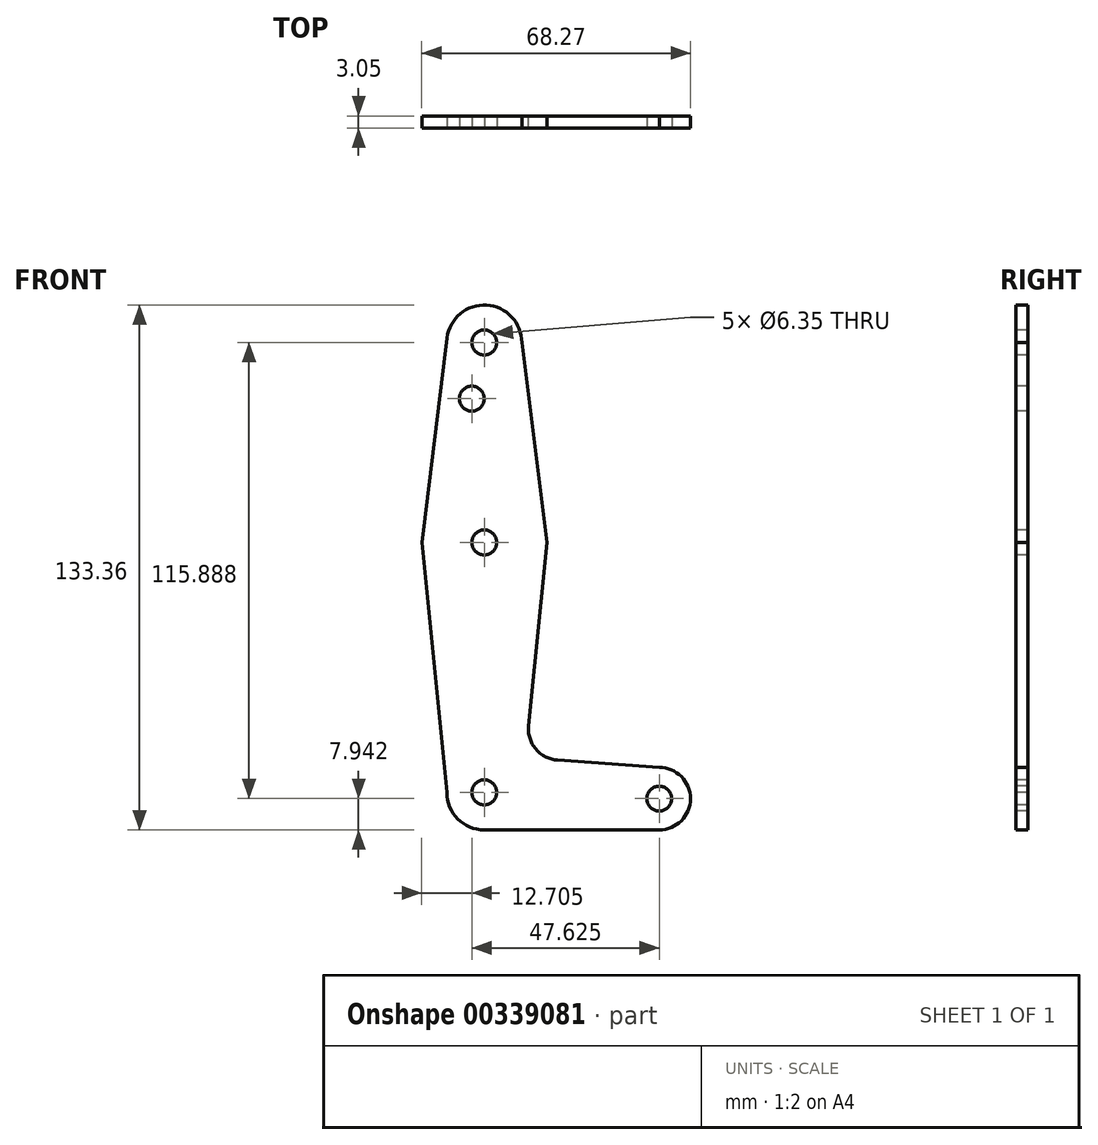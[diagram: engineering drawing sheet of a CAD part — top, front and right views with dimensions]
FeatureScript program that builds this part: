
annotation { "Feature Type Name" : "Feature", "Feature Type Description" : "" }
export const myFeature = defineFeature(function(context is Context, id is Id, definition is map)
    precondition{}
    {
        {
            var Q0;
            Q0=qCreatedBy(makeId("Front.planeOp"),FACE);
            var sketch = newSketch(context, id + "F0", { "sketchPlane" : qUnion([Q0])});
            skCircle(sketch, "E0", {"center": v(0, 0) * mm, "radius": 9.53 * mm});
            skCircle(sketch, "E1", {"center": v(0, 63.5) * mm, "radius": 15.88 * mm});
            skCircle(sketch, "E2", {"center": v(0, 114.3) * mm, "radius": 9.53 * mm});
            skCircle(sketch, "E3", {"center": v(44.45, -1.59) * mm, "radius": 7.94 * mm});
            skLineSegment(sketch, "E4", {"start": v(-15.87, 63.5) * mm, "end": v(-9.52, 0) * mm});
            skLineSegment(sketch, "E5", {"start": v(15.88, 63.5) * mm, "end": v(9.48, -0.94) * mm});
            skLineSegment(sketch, "E6", {"start": v(-15.87, 63.5) * mm, "end": v(-9.45, 115.47) * mm});
            skLineSegment(sketch, "E7", {"start": v(15.88, 63.5) * mm, "end": v(9.52, 114.3) * mm});
            skLineSegment(sketch, "E8", {"start": v(0.68, 9.5) * mm, "end": v(44.45, 6.35) * mm});
            skLineSegment(sketch, "E9", {"start": v(0, -9.53) * mm, "end": v(44.45, -9.52) * mm});
            skCircle(sketch, "E10", {"center": v(0, 114.3) * mm, "radius": 3.18 * mm});
            skCircle(sketch, "E11", {"center": v(0, 0) * mm, "radius": 3.18 * mm});
            skCircle(sketch, "E12", {"center": v(44.45, -1.59) * mm, "radius": 3.18 * mm});
            skCircle(sketch, "E13", {"center": v(0, 63.5) * mm, "radius": 3.18 * mm});
            skPoint(sketch, "E14.center.orphan", {"position": v(-3.18, 100.03) * mm});
            skCircle(sketch, "E15", {"center": v(-3.18, 100.03) * mm, "radius": 3.18 * mm});
            skLineSegment(sketch, "E16", {"start": v(0, 63.5) * mm, "end": v(0, 66.67) * mm});
            skSolve(sketch);
        }
        {
            var Q0;
            Q0=makeQuery(id+"F0.imprint","IMPRINT",FACE,{"disambiguationData":[TD([[makeQuery(id+"F0.imprint","IMPRINT",EDGE,{"derivedFrom":sQuery(id+"F0.wireOp",EDGE,"E15")}),-1.0]])]});
            var Q1;
            Q1=makeQuery(id+"F0.imprint","IMPRINT",FACE,{"disambiguationData":[TD([[makeQuery(id+"F0.imprint","IMPRINT",EDGE,{"derivedFrom":sQuery(id+"F0.wireOp",EDGE,"E10")}),-1.0]])]});
            var Q2;
            Q2=makeQuery(id+"F0.imprint","IMPRINT",FACE,{"disambiguationData":[TD([[makeQuery(id+"F0.imprint","IMPRINT",EDGE,{"derivedFrom":sQuery(id+"F0.wireOp",EDGE,"E13")}),-1.0]])]});
            var Q3;
            {var subQ5=sQuery(id+"F0.wireOp",EDGE,"E4");var subQ7=sQuery(id+"F0.wireOp",EDGE,"E0");var subQ8=makeQuery(id+"F0.imprint","INTERSECT",VERTEX,{"derivedFrom":[subQ7,subQ5]});Q3=makeQuery(id+"F0.imprint","IMPRINT",FACE,{"disambiguationData":[TD([[makeQuery(id+"F0.imprint","IMPRINT",EDGE,{"disambiguationData":[TD([[subQ8,1.0]])],"derivedFrom":subQ7}),-1.0]])]});}
            var Q4;
            {var subQ7=sQuery(id+"F0.wireOp",EDGE,"E9");Q4=makeQuery(id+"F0.imprint","IMPRINT",FACE,{"disambiguationData":[TD([[makeQuery(id+"F0.imprint","IMPRINT",EDGE,{"derivedFrom":subQ7}),1.0]])]});}
            var Q5;
            Q5=makeQuery(id+"F0.imprint","IMPRINT",FACE,{"disambiguationData":[TD([[makeQuery(id+"F0.imprint","IMPRINT",EDGE,{"derivedFrom":sQuery(id+"F0.wireOp",EDGE,"E12")}),-1.0]])]});
            var Q6;
            Q6=makeQuery(id+"F0.imprint","IMPRINT",FACE,{"disambiguationData":[TD([[makeQuery(id+"F0.imprint","IMPRINT",EDGE,{"derivedFrom":sQuery(id+"F0.wireOp",EDGE,"E11")}),-1.0]])]});
            var Q7;
            {var subQ0=sQuery(id+"F0.wireOp",EDGE,"E5");var subQ1=sQuery(id+"F0.wireOp",EDGE,"E0");var subQ2=makeQuery(id+"F0.imprint","INTERSECT",VERTEX,{"derivedFrom":[subQ1,subQ0]});Q7=makeQuery(id+"F0.imprint","IMPRINT",FACE,{"disambiguationData":[TD([[makeQuery(id+"F0.imprint","IMPRINT",EDGE,{"disambiguationData":[TD([[subQ2,-1.0]])],"derivedFrom":subQ1}),-1.0]])]});}
            extrude(context, id + "F1", {"entities" : qUnion([Q0, Q1, Q2, Q3, Q4, Q5, Q6, Q7]), "oppositeDirection" : true, "depth" : 3.05 * mm});
        }
        {
            var Q0;
            Q0=makeQuery(id+"F1.opExtrude","SWEPT_EDGE",EDGE,{"disambiguationData":[OSD([sQuery(id+"F0.wireOp",EDGE,"E5"),sQuery(id+"F0.wireOp",EDGE,"E8")])]});
            fillet(context, id + "F2", {"entities" : qUnion([Q0]), "radius" : 7.95 * mm, "tangentPropagation" : true, "allowEdgeOverflow" : false});
        }
    });
